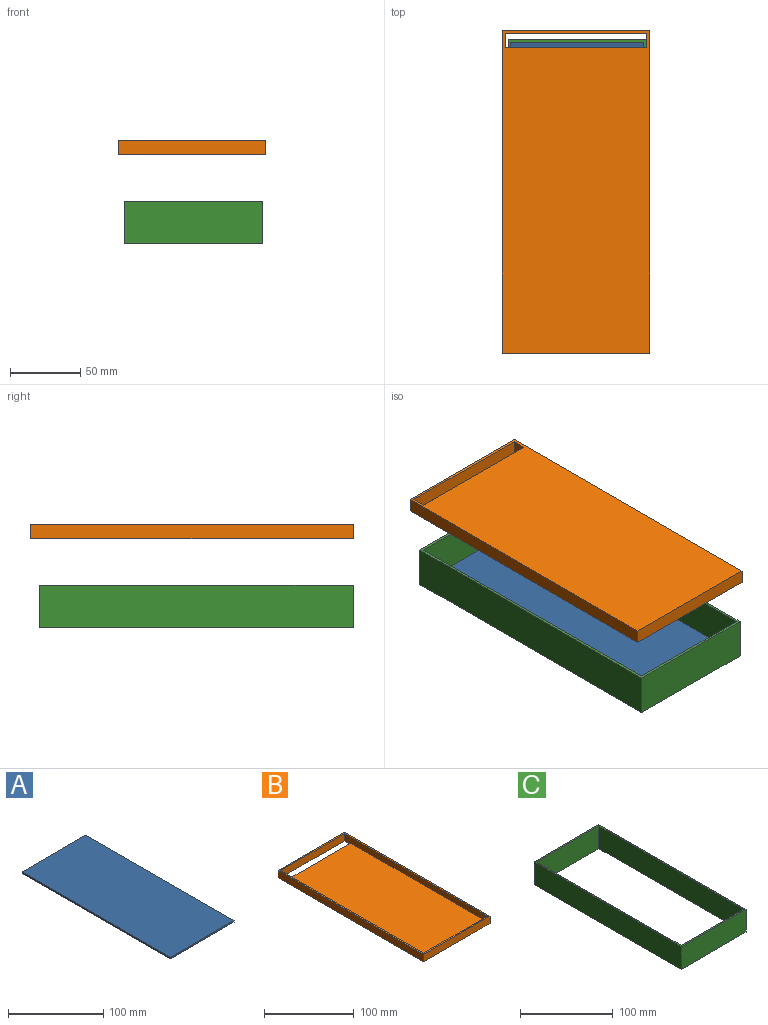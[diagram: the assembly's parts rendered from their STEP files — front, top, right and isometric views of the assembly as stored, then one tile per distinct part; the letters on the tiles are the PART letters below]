
ASSEMBLY  parts=3 mates=6
PART A: 6 faces, bbox 95x220x2 mm
  f0: plane 95x2mm, normal (0,-1,0), area 190mm2, adj f1,f3,f4,f5
  f1: plane 220x2mm, normal (1,0,0), area 440mm2, adj f0,f2,f4,f5
  f2: plane 95x2mm, normal (0,1,0), area 190mm2, adj f1,f3,f4,f5
  f3: plane 220x2mm, normal (-1,0,0), area 440mm2, adj f0,f2,f4,f5
  f4: plane 220x95mm, normal (0,0,1), area 20900mm2, adj f0,f1,f2,f3
  f5: plane 220x95mm, normal (0,0,-1), area 20900mm2, adj f0,f1,f2,f3
PART B: 12 faces, bbox 105x230x10 mm
  f0: plane 230x105mm, normal (0,0,-1), area 23140mm2, adj f1,f2,f3,f4,f6,f7,f8,f11
  f1: plane 230x10mm, normal (-1,0,0), area 2300mm2, adj f0,f2,f8,f9
  f2: plane 105x10mm, normal (0,-1,0), area 1050mm2, adj f0,f1,f3,f9
  f3: plane 230x10mm, normal (1,0,0), area 2300mm2, adj f0,f2,f8,f9
  f4: plane 226x10mm, normal (-1,0,0), area 1828mm2, adj f0,f5,f7,f9,f10,f11
  f5: plane 101x8mm, normal (0,1,0), area 808mm2, adj f4,f6,f9,f10
  f6: plane 226x10mm, normal (1,0,0), area 1828mm2, adj f0,f5,f7,f9,f10,f11
  f7: plane 101x10mm, normal (0,-1,0), area 1010mm2, adj f0,f4,f6,f9
  f8: plane 105x10mm, normal (0,1,0), area 1050mm2, adj f0,f1,f3,f9
  f9: plane 230x105mm, normal (0,0,1), area 1324mm2, adj f1,f2,f3,f4,f5,f6,f7,f8
  f10: plane 216x101mm, normal (0,0,1), area 21816mm2, adj f4,f5,f6,f11
  f11: plane 101x2mm, normal (0,1,0), area 202mm2, adj f0,f4,f6,f10
PART C: 10 faces, bbox 99x224x30 mm
  f0: plane 224x30mm, normal (1,0,0), area 6720mm2, adj f1,f7,f8,f9
  f1: plane 99x30mm, normal (0,1,0), area 2970mm2, adj f0,f2,f8,f9
  f2: plane 224x30mm, normal (-1,0,0), area 6720mm2, adj f1,f7,f8,f9
  f3: plane 220x30mm, normal (-1,0,0), area 6600mm2, adj f4,f6,f8,f9
  f4: plane 95x30mm, normal (0,1,0), area 2850mm2, adj f3,f5,f8,f9
  f5: plane 220x30mm, normal (1,0,0), area 6600mm2, adj f4,f6,f8,f9
  f6: plane 95x30mm, normal (0,-1,0), area 2850mm2, adj f3,f5,f8,f9
  f7: plane 99x30mm, normal (0,-1,0), area 2970mm2, adj f0,f2,f8,f9
  f8: plane 224x99mm, normal (0,0,1), area 1276mm2, adj f0,f1,f2,f3,f4,f5,f6,f7
  f9: plane 224x99mm, normal (0,0,-1), area 1276mm2, adj f0,f1,f2,f3,f4,f5,f6,f7
PLACE A t=(6.72,-13.4,-11.93)mm
PLACE B rot(axis=(0,1,0),180deg) t=(5.72,-10.4,61.28)mm
PLACE C t=(6.72,-13.4,-11.93)mm
MATE parallel B.f10 <-> A.f4  axis (0,0,-1) through (5.72,-15.4,59.28)mm
MATE planar B.f6 <-> C.f0  axis (-1,0,0) through (56.22,-9.22,55.34)mm
MATE planar B.f5 <-> C.f4  axis (0,1,0) through (5.72,-123.4,59.28)mm
MATE planar A.f5 <-> C.f9  axis (0,0,-1) through (6.72,-13.4,-11.93)mm
MATE planar A.f1 <-> C.f3  axis (1,0,0) through (54.22,-13.4,-10.93)mm
MATE planar A.f0 <-> C.f4  axis (0,-1,0) through (6.72,-123.4,-10.93)mm
